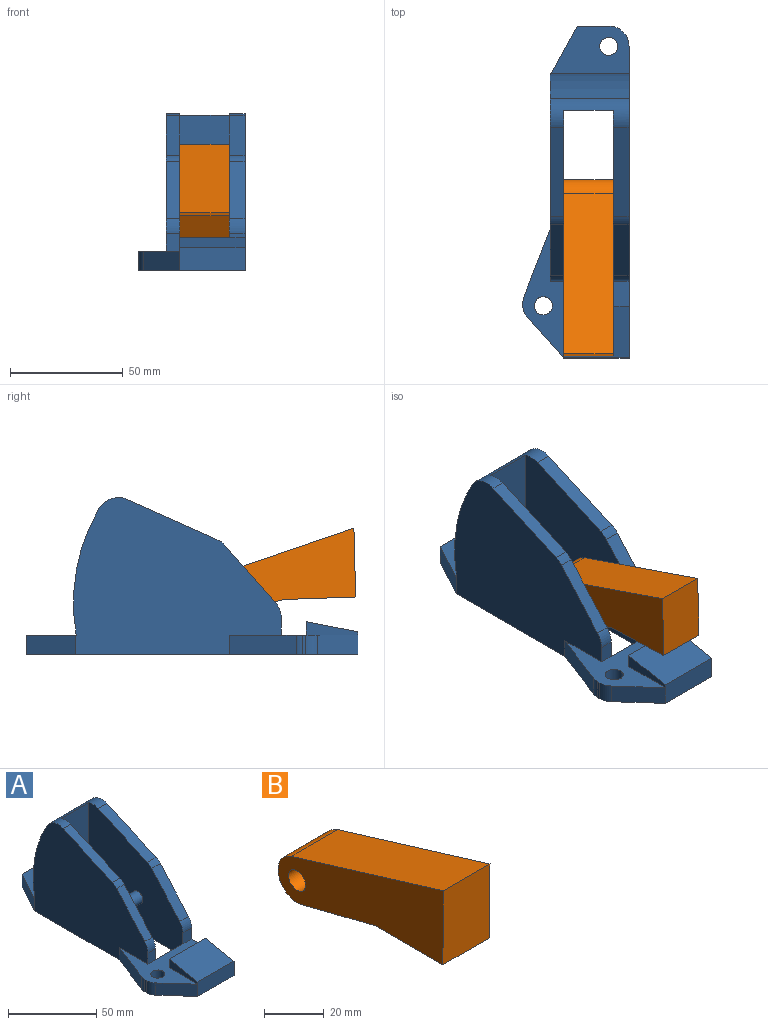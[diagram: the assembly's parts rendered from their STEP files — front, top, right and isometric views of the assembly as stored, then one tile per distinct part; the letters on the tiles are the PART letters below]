
ASSEMBLY  parts=2 mates=1
PART A: 36 faces, bbox 47x147x69.4 mm
  f0: plane 39.58x17.66mm, normal (0,-0.41,0.91), area 303.4mm2, adj f7,f28,f31,f33
  f1: plane 57x47mm, normal (0,0,1), area 788.2mm2, adj f5,f7,f11,f12,f13,f14,f17,f18
  f2: plane 147x47mm, normal (0,0,-1), area 3547.2mm2, adj f7,f8,f9,f10,f11,f12,f13,f14
  f3: plane 39.58x17.66mm, normal (0,-0.41,0.91), area 260.1mm2, adj f11,f27,f33,f34
  f4: plane 25.53x22.52mm, normal (0,-0.75,0.66), area 204.3mm2, adj f11,f27,f34,f35
  f5: plane 7.72x6mm, normal (0,-1,0), area 46.3mm2, adj f1,f11,f27,f35
  f6: plane 35x22.23mm, normal (0,0,1), area 578.4mm2, adj f7,f8,f9,f10,f11,f16,f23
  f7: plane 138x69.41mm, normal (1,0,0), area 5301.8mm2, adj f0,f1,f2,f6,f8,f15,f21,f22
  f8: cylinder r=9mm len=9mm, axis (0,0,-1), area 120.2mm2, adj f2,f6,f7,f9
  f9: plane 14x8.5mm, normal (0,1,0), area 119mm2, adj f2,f6,f8,f10
  f10: plane 22x12mm, normal (-0.88,0.48,0), area 213mm2, adj f2,f6,f9,f11
  f11: plane 92x69.41mm, normal (-1,0,0), area 4620.5mm2, adj f1,f2,f3,f4,f5,f6,f10,f12
  f12: plane 29.61x11.46mm, normal (-0.93,0.36,0), area 269.9mm2, adj f1,f2,f11,f18
  f13: plane 8.5x1.44mm, normal (-1,0,0), area 12.2mm2, adj f1,f2,f18,f19
  f14: plane 17.72x15.95mm, normal (-0.74,-0.67,0), area 202.6mm2, adj f1,f2,f15,f19
  f15: plane 29x10mm, normal (0,-1,0), area 290mm2, adj f2,f7,f14,f20,f22
  f16: cylinder r=4mm len=8.5mm, axis (0,0,-1), area 213.6mm2, adj f2,f6
  f17: cylinder r=4mm len=8.5mm, axis (0,0,-1), area 213.6mm2, adj f1,f2
  f18: cylinder r=8mm len=8.5mm, axis (0,0,-1), area 25.1mm2, adj f1,f2,f12,f13
  f19: cylinder r=8mm len=8.5mm, axis (0,0,-1), area 49.8mm2, adj f1,f2,f13,f14
  f20: plane 23x6mm, normal (-1,0,0), area 86.2mm2, adj f1,f15,f21,f22
  f21: plane 29x6mm, normal (0,1,0), area 174mm2, adj f1,f7,f20,f22
  f22: plane 29x23mm, normal (0,-0.19,0.98), area 679.6mm2, adj f7,f15,f20,f21
  f23: cylinder r=82.9mm len=55.94mm, axis (1,0,0), area 2030.4mm2, adj f6,f7,f11,f33
  f24: plane 25.53x22.52mm, normal (0,-0.75,0.66), area 238.3mm2, adj f7,f28,f31,f32
  f25: plane 7.72x7mm, normal (0,-1,0), area 54mm2, adj f1,f7,f28,f32
  f26: plane 68.78x22mm, normal (0,-1,0), area 1513.1mm2, adj f2,f27,f28,f33
  f27: plane 75.66x69.41mm, normal (1,0,0), area 3862.4mm2, adj f1,f2,f3,f4,f5,f26,f29,f30
  f28: plane 75.66x69.41mm, normal (-1,0,0), area 3862.4mm2, adj f0,f1,f2,f24,f25,f26,f29,f30
  f29: plane 22x8.5mm, normal (0,1,0), area 187mm2, adj f1,f2,f27,f28
  f30: cylinder r=4mm len=22mm, axis (1,0,0), area 552.9mm2, adj f27,f28
  f31: cylinder r=10mm len=7mm, axis (1,0,0), area 30mm2, adj f0,f7,f24,f28
  f32: cylinder r=10mm len=7mm, axis (1,0,0), area 50.6mm2, adj f7,f24,f25,f28
  f33: cylinder r=10mm len=35mm, axis (1,0,0), area 341mm2, adj f0,f3,f7,f11,f23,f26,f27,f28
  f34: cylinder r=10mm len=6mm, axis (1,0,0), area 25.7mm2, adj f3,f4,f11,f27
  f35: cylinder r=10mm len=6.61mm, axis (1,0,0), area 43.4mm2, adj f4,f5,f11,f27
PART B: 8 faces, bbox 22x78.3x39.5 mm
  f0: plane 71.92x22mm, normal (0,0.29,0.96), area 1653.7mm2, adj f1,f5,f6,f7
  f1: plane 30.46x22mm, normal (0,-1,-0.01), area 670.2mm2, adj f0,f2,f6,f7
  f2: plane 32x22mm, normal (0,0,-1), area 704mm2, adj f1,f3,f6,f7
  f3: plane 34.81x22mm, normal (0,-0.24,-0.97), area 789.6mm2, adj f2,f5,f6,f7
  f4: cylinder r=4mm len=22mm, axis (1,0,0), area 552.9mm2, adj f6,f7
  f5: cylinder r=9mm len=22mm, axis (1,0,0), area 612.3mm2, adj f0,f3,f6,f7
  f6: plane 78.31x39.46mm, normal (-1,0,0), area 1625.6mm2, adj f0,f1,f2,f3,f4,f5
  f7: plane 78.31x39.46mm, normal (1,0,0), area 1625.6mm2, adj f0,f1,f2,f3,f4,f5
PLACE A t=(3,33.9,0)mm
PLACE B rot(axis=(-1,0,0),2deg) t=(31,33.58,5.17)mm
MATE revolute B.f4 <-> A.f30  axis (1,0,0) through (31,46.9,23)mm
